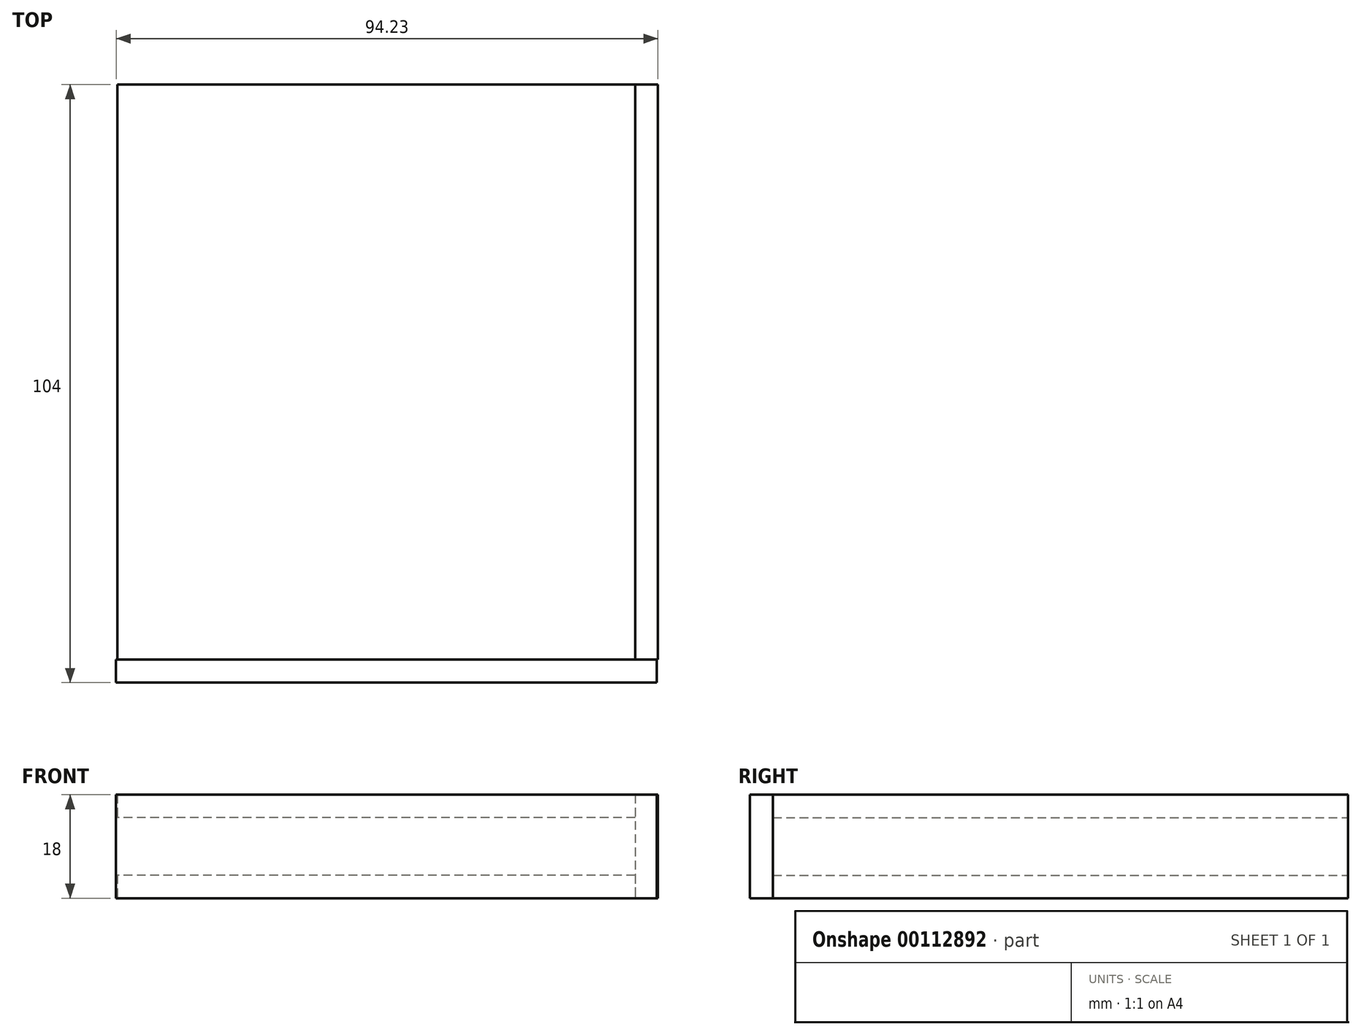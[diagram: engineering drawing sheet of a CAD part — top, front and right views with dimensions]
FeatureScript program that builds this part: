
annotation { "Feature Type Name" : "Feature", "Feature Type Description" : "" }
export const myFeature = defineFeature(function(context is Context, id is Id, definition is map)
    precondition{}
    {
        {
            var Q0;
            Q0=qCreatedBy(makeId("Top.planeOp"),FACE);
            var sketch = newSketch(context, id + "F0", { "sketchPlane" : qUnion([Q0])});
            skLineSegment(sketch, "E0.bottom", {"start": v(0, 0) * mm, "end": v(-90, 0) * mm});
            skLineSegment(sketch, "E0.top", {"start": v(0, 100) * mm, "end": v(-90, 100) * mm});
            skLineSegment(sketch, "E0.left", {"start": v(0, 0) * mm, "end": v(0, 100) * mm});
            skLineSegment(sketch, "E0.right", {"start": v(-90, 0) * mm, "end": v(-90, 100) * mm});
            skSolve(sketch);
        }
        {
            var Q0;
            Q0=makeQuery(id+"F0.imprint","IMPRINT",FACE,{"disambiguationData":[TD([[makeQuery(id+"F0.imprint","IMPRINT",EDGE,{"derivedFrom":sQuery(id+"F0.wireOp",EDGE,"E0.bottom")}),-1.0]])]});
            extrude(context, id + "F1", {"entities" : qUnion([Q0]), "depth" : 4 * mm});
        }
        {
            var Q0;
            Q0=makeQuery(id+"F1.opExtrude","CAP_FACE",FACE,{"disambiguationData":[OSD([sQuery(id+"F0.wireOp",EDGE,"E0.bottom"),sQuery(id+"F0.wireOp",EDGE,"E0.top"),sQuery(id+"F0.wireOp",EDGE,"E0.left"),sQuery(id+"F0.wireOp",EDGE,"E0.right")])],"isStart":false});
            cPlane(context, id + "F2", {"entities" : qUnion([Q0]), "cplaneType" : CPlaneType.OFFSET, "offset" : 10 * mm, "width" : 150 * mm, "height" : 150 * mm});
        }
        {
            var Q0;
            Q0=qCreatedBy(id+"F2.planeOp",FACE);
            var sketch = newSketch(context, id + "F3", { "sketchPlane" : qUnion([Q0])});
            skLineSegment(sketch, "E1.bottom", {"start": v(0, 0) * mm, "end": v(-90, 0) * mm});
            skLineSegment(sketch, "E1.top", {"start": v(0, 100) * mm, "end": v(-90, 100) * mm});
            skLineSegment(sketch, "E1.left", {"start": v(0, 0) * mm, "end": v(0, 100) * mm});
            skLineSegment(sketch, "E1.right", {"start": v(-90, 0) * mm, "end": v(-90, 100) * mm});
            skSolve(sketch);
        }
        {
            var Q0;
            Q0=makeQuery(id+"F3.imprint","IMPRINT",FACE,{"disambiguationData":[TD([[makeQuery(id+"F3.imprint","IMPRINT",EDGE,{"derivedFrom":sQuery(id+"F3.wireOp",EDGE,"E1.bottom")}),-1.0]])]});
            extrude(context, id + "F4", {"entities" : qUnion([Q0]), "depth" : 4 * mm});
        }
        {
            var Q0;
            Q0=qCreatedBy(makeId("Right.planeOp"),FACE);
            var sketch = newSketch(context, id + "F5", { "sketchPlane" : qUnion([Q0])});
            skLineSegment(sketch, "E2.bottom", {"start": v(0, 18) * mm, "end": v(100, 18) * mm});
            skLineSegment(sketch, "E2.top", {"start": v(0, 0) * mm, "end": v(100, 0) * mm});
            skLineSegment(sketch, "E2.left", {"start": v(0, 18) * mm, "end": v(0, 0) * mm});
            skLineSegment(sketch, "E2.right", {"start": v(100, 18) * mm, "end": v(100, 0) * mm});
            skSolve(sketch);
        }
        {
            var Q0;
            Q0=makeQuery(id+"F5.imprint","IMPRINT",FACE,{"disambiguationData":[TD([[makeQuery(id+"F5.imprint","IMPRINT",EDGE,{"derivedFrom":sQuery(id+"F5.wireOp",EDGE,"E2.bottom")}),-1.0]])]});
            extrude(context, id + "F6", {"entities" : qUnion([Q0]), "depth" : 4 * mm});
        }
        {
            var Q0;
            Q0=qCreatedBy(makeId("Front.planeOp"),FACE);
            var sketch = newSketch(context, id + "F7", { "sketchPlane" : qUnion([Q0])});
            skLineSegment(sketch, "E3.bottom", {"start": v(3.77, 0) * mm, "end": v(-90.23, 0) * mm});
            skLineSegment(sketch, "E3.top", {"start": v(3.77, 18) * mm, "end": v(-90.23, 18) * mm});
            skLineSegment(sketch, "E3.left", {"start": v(3.77, 0) * mm, "end": v(3.77, 18) * mm});
            skLineSegment(sketch, "E3.right", {"start": v(-90.23, 0) * mm, "end": v(-90.23, 18) * mm});
            skSolve(sketch);
        }
        {
            var Q0;
            Q0=makeQuery(id+"F7.imprint","IMPRINT",FACE,{"disambiguationData":[TD([[makeQuery(id+"F7.imprint","IMPRINT",EDGE,{"derivedFrom":sQuery(id+"F7.wireOp",EDGE,"E3.bottom")}),-1.0]])]});
            extrude(context, id + "F8", {"entities" : qUnion([Q0]), "depth" : 4 * mm});
        }
    });
